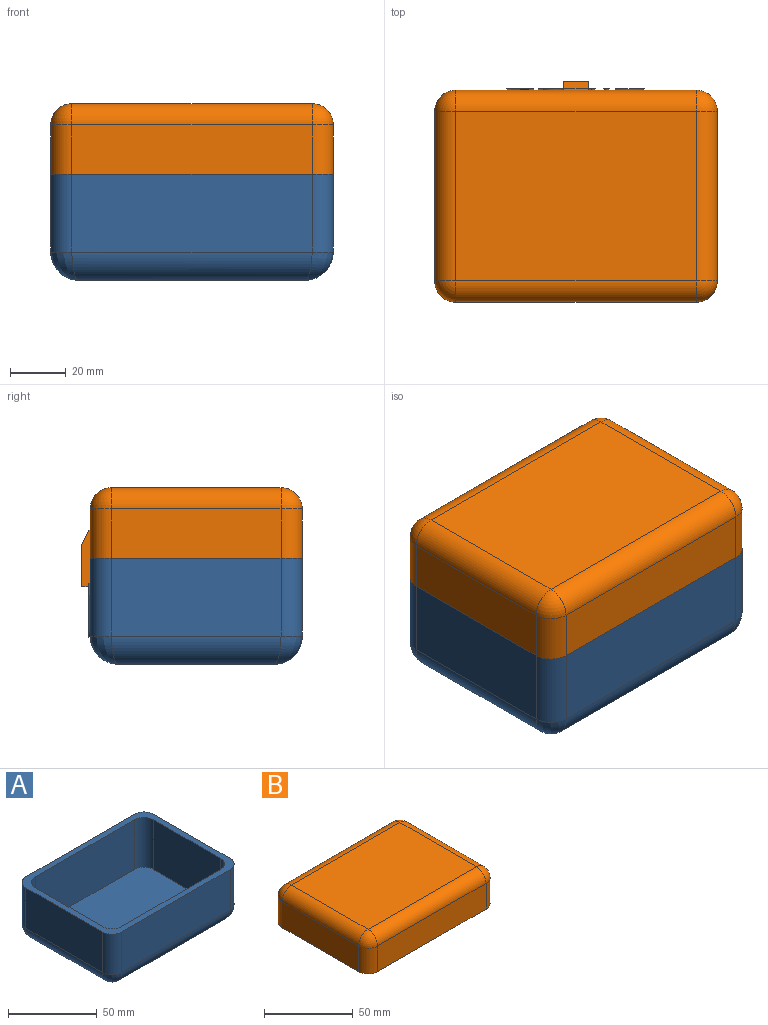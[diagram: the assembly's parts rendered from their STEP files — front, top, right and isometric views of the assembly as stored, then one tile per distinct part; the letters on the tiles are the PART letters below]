
ASSEMBLY  parts=2 mates=1
PART A: 121 faces, bbox 101.6x76.8x38.1 mm
  f0: plane 60.96x27.94mm, normal (1,0,0), area 1703.2mm2, adj f4,f11,f14,f22
  f1: plane 86.36x27.95mm, normal (0,1,0), area 2159.4mm2, adj f4,f11,f12,f19,f27,f29,f30,f31
  f2: plane 60.96x27.94mm, normal (-1,0,0), area 1703.2mm2, adj f4,f12,f13,f23
  f3: plane 86.36x27.94mm, normal (0,-1,0), area 2412.9mm2, adj f4,f13,f14,f26
  f4: plane 101.6x76.2mm, normal (0,0,1), area 1296.8mm2, adj f0,f1,f2,f3,f6,f7,f8,f9
  f5: plane 81.28x55.88mm, normal (0,0,-1), area 4541.9mm2, adj f19,f22,f23,f26
  f6: plane 53.34x34.29mm, normal (-1,0,0), area 1829mm2, adj f4,f10,f16,f18
  f7: plane 78.74x34.29mm, normal (0,-1,0), area 2700mm2, adj f4,f10,f17,f18
  f8: plane 53.34x34.29mm, normal (1,0,0), area 1829mm2, adj f4,f10,f15,f17
  f9: plane 78.74x34.29mm, normal (0,1,0), area 2700mm2, adj f4,f10,f15,f16
  f10: plane 93.98x68.58mm, normal (0,0,1), area 6395.3mm2, adj f6,f7,f8,f9,f15,f16,f17,f18
  f11: cylinder r=7.62mm len=27.94mm, axis (0,0,-1), area 334.4mm2, adj f0,f1,f4,f20
  f12: cylinder r=7.62mm len=27.94mm, axis (0,0,1), area 334.4mm2, adj f1,f2,f4,f21
  f13: cylinder r=7.62mm len=27.94mm, axis (0,0,-1), area 334.4mm2, adj f2,f3,f4,f25
  f14: cylinder r=7.62mm len=27.94mm, axis (0,0,1), area 334.4mm2, adj f0,f3,f4,f24
  f15: cylinder r=7.62mm len=34.29mm, axis (0,0,1), area 410.4mm2, adj f4,f8,f9,f10
  f16: cylinder r=7.62mm len=34.29mm, axis (0,0,-1), area 410.4mm2, adj f4,f6,f9,f10
  f17: cylinder r=7.62mm len=34.29mm, axis (0,0,-1), area 410.4mm2, adj f4,f7,f8,f10
  f18: cylinder r=7.62mm len=34.29mm, axis (0,0,1), area 410.4mm2, adj f4,f6,f7,f10
  f19: cylinder r=10.16mm len=86.36mm, axis (-1,0,0), area 1348.8mm2, adj f1,f5,f20,f21,f103
  f20: bspline ~12.46x10.16mm, area 124.7mm2, adj f11,f19,f22
  f21: bspline ~12.46x10.16mm, area 124.7mm2, adj f12,f19,f23
  f22: cylinder r=10.16mm len=60.96mm, axis (0,1,0), area 943.4mm2, adj f0,f5,f20,f24
  f23: cylinder r=10.16mm len=60.96mm, axis (0,-1,0), area 943.4mm2, adj f2,f5,f21,f25
  f24: bspline ~12.46x10.16mm, area 124.7mm2, adj f14,f22,f26
  f25: bspline ~12.46x10.16mm, area 124.7mm2, adj f13,f23,f26
  f26: cylinder r=10.16mm len=86.36mm, axis (1,0,0), area 1348.8mm2, adj f3,f5,f24,f25
  f27: cone r=2.54mm half-angle=35deg, axis (0,1,0), area 20.4mm2, adj f1,f28
  f28: plane 3.3x3.3mm, normal (0,1,0), area 8.6mm2, adj f27
  f29: extruded ~3.14x0.73mm, area 2.1mm2, adj f1,f30,f43,f44
  f30: plane 1.38x0.68mm, normal (-0.9,0,-0.44), area 1mm2, adj f1,f29,f31,f44
  f31: extruded ~3.8x0.79mm, area 2.5mm2, adj f1,f30,f32,f44
  f32: extruded ~3.55x0.87mm, area 2.3mm2, adj f1,f31,f33,f44
  f33: extruded ~2.47x2.3mm, area 2.2mm2, adj f1,f32,f34,f44
  f34: extruded ~3.74x0.8mm, area 2.4mm2, adj f1,f33,f35,f44
  f35: extruded ~5.26x1.66mm, area 3.6mm2, adj f1,f34,f36,f44
  f36: extruded ~4.71x1.85mm, area 3.3mm2, adj f1,f35,f37,f44
  f37: extruded ~3.54x0.64mm, area 2.3mm2, adj f1,f36,f38,f44
  f38: plane 1.41x0.64mm, normal (-1,0,0), area 0.9mm2, adj f1,f37,f39,f44
  f39: extruded ~3.3x0.64mm, area 2.1mm2, adj f1,f38,f40,f44
  f40: extruded ~3.62x1.48mm, area 2.6mm2, adj f1,f39,f41,f44
  f41: extruded ~4.19x1.27mm, area 2.8mm2, adj f1,f40,f42,f44
  f42: extruded ~4.15x1.32mm, area 2.8mm2, adj f1,f41,f43,f44
  f43: extruded ~3.59x1.52mm, area 2.6mm2, adj f1,f29,f42,f44
  f44: plane 14.2x10.45mm, normal (0,1,0), area 41.7mm2, adj f29,f30,f31,f32,f33,f34,f35,f36
  f45: plane 10.35x0.64mm, normal (-1,0,0), area 6.6mm2, adj f1,f46,f48,f49
  f46: plane 1.57x0.64mm, normal (0,0,1), area 1mm2, adj f1,f45,f47,f49
  f47: plane 10.35x0.64mm, normal (1,0,0), area 6.6mm2, adj f1,f46,f48,f49
  f48: plane 1.57x0.64mm, normal (0,0,-1), area 1mm2, adj f1,f45,f47,f49
  f49: plane 10.35x1.57mm, normal (0,1,0), area 16.2mm2, adj f45,f46,f47,f48
  f50: extruded ~0.79x0.64mm, area 0.5mm2, adj f1,f51,f57,f58
  f51: extruded ~0.66x0.64mm, area 0.5mm2, adj f1,f50,f52,f58
  f52: extruded ~0.65x0.64mm, area 0.5mm2, adj f1,f51,f53,f58
  f53: extruded ~0.79x0.64mm, area 0.5mm2, adj f1,f52,f54,f58
  f54: extruded ~0.78x0.64mm, area 0.5mm2, adj f1,f53,f55,f58
  f55: extruded ~0.65x0.64mm, area 0.5mm2, adj f1,f54,f56,f58
  f56: extruded ~0.66x0.64mm, area 0.5mm2, adj f1,f55,f57,f58
  f57: extruded ~0.79x0.64mm, area 0.5mm2, adj f1,f50,f56,f58
  f58: plane 2.09x1.85mm, normal (0,1,0), area 3.2mm2, adj f50,f51,f52,f53,f54,f55,f56,f57
  f59: plane 1.57x0.64mm, normal (0,0,-1), area 1mm2, adj f1,f60,f75,f76
  f60: plane 6.75x0.64mm, normal (-1,0,0), area 4.3mm2, adj f1,f59,f61,f76
  f61: extruded ~2.89x0.94mm, area 2mm2, adj f1,f60,f62,f76
  f62: extruded ~2.82x0.9mm, area 1.9mm2, adj f1,f61,f63,f76
  f63: extruded ~1.94x0.64mm, area 1.3mm2, adj f1,f62,f64,f76
  f64: extruded ~1.35x1.19mm, area 1.2mm2, adj f1,f63,f65,f76
  f65: plane 0.64x0.08mm, normal (0,0,1), area 0mm2, adj f1,f64,f66,f76
  f66: plane 1.42x0.64mm, normal (-0.98,0,0.18), area 0.9mm2, adj f1,f65,f67,f76
  f67: plane 1.28x0.64mm, normal (0,0,1), area 0.8mm2, adj f1,f66,f68,f76
  f68: plane 10.35x0.64mm, normal (1,0,0), area 6.6mm2, adj f1,f67,f69,f76
  f69: plane 1.57x0.64mm, normal (0,0,-1), area 1mm2, adj f1,f68,f70,f76
  f70: plane 5.43x0.64mm, normal (-1,0,0), area 3.4mm2, adj f1,f69,f71,f76
  f71: extruded ~2.9x0.76mm, area 1.9mm2, adj f1,f70,f72,f76
  f72: extruded ~2.38x0.88mm, area 1.7mm2, adj f1,f71,f73,f76
  f73: extruded ~1.81x0.64mm, area 1.2mm2, adj f1,f72,f74,f76
  f74: extruded ~1.89x0.64mm, area 1.3mm2, adj f1,f73,f75,f76
  f75: plane 6.7x0.64mm, normal (1,0,0), area 4.3mm2, adj f1,f59,f74,f76
  f76: plane 10.54x8.65mm, normal (0,1,0), area 38.8mm2, adj f59,f60,f61,f62,f63,f64,f65,f66
  f77: plane 1.39x0.64mm, normal (0.99,0,-0.15), area 0.9mm2, adj f1,f78,f100,f101
  f78: plane 1.28x0.64mm, normal (0,0,-1), area 0.8mm2, adj f1,f77,f79,f101
  f79: plane 14.7x0.64mm, normal (-1,0,0), area 9.3mm2, adj f1,f78,f80,f101
  f80: plane 1.57x0.64mm, normal (0,0,1), area 1mm2, adj f1,f79,f81,f101
  f81: plane 4.21x0.64mm, normal (1,0,0), area 2.7mm2, adj f1,f80,f82,f101
  f82: plane 0.73x0.64mm, normal (1,0,-0.05), area 0.5mm2, adj f1,f81,f83,f101
  f83: plane 0.75x0.64mm, normal (1,0,-0.09), area 0.5mm2, adj f1,f82,f84,f101
  f84: plane 0.64x0.12mm, normal (0,0,1), area 0.1mm2, adj f1,f83,f85,f101
  f85: extruded ~3.23x1.53mm, area 2.4mm2, adj f1,f84,f86,f101
  f86: extruded ~3.16x1.42mm, area 2.3mm2, adj f1,f85,f87,f101
  f87: extruded ~3.98x1.13mm, area 2.7mm2, adj f1,f86,f88,f101
  f88: extruded ~3.95x1.13mm, area 2.7mm2, adj f1,f87,f89,f101
  f89: extruded ~3.16x1.39mm, area 2.3mm2, adj f1,f88,f90,f101
  f90: extruded ~3.25x1.58mm, area 2.4mm2, adj f1,f89,f100,f101
  f91: extruded ~2.14x1.01mm, area 1.6mm2, adj f92,f99,f101,f102
  f92: extruded ~2.99x0.73mm, area 2mm2, adj f91,f93,f101,f102
  f93: extruded ~3.03x0.73mm, area 2mm2, adj f92,f94,f101,f102
  f94: extruded ~2.11x1.07mm, area 1.6mm2, adj f93,f95,f101,f102
  f95: extruded ~2.34x0.94mm, area 1.7mm2, adj f94,f96,f101,f102
  f96: extruded ~3.14x0.73mm, area 2.1mm2, adj f95,f97,f101,f102
  f97: plane 0.64x0.33mm, normal (1,0,0), area 0.2mm2, adj f96,f98,f101,f102
  f98: extruded ~2.82x0.72mm, area 1.9mm2, adj f97,f99,f101,f102
  f99: extruded ~2.33x0.87mm, area 1.6mm2, adj f91,f98,f101,f102
  f100: plane 0.64x0.08mm, normal (0,0,-1), area 0.1mm2, adj f1,f77,f90,f101
  f101: plane 14.89x9.11mm, normal (0,1,0), area 52.2mm2, adj f77,f78,f79,f80,f81,f82,f83,f84
  f102: plane 8.1x5.91mm, normal (0,1,0), area 40.3mm2, adj f91,f92,f93,f94,f95,f96,f97,f98
  f103: plane 3.03x0.38mm, normal (0,-1,0), area 0.8mm2, adj f19,f104,f105,f106
  f104: plane 1.25x0.64mm, normal (1,0,0), area 0.8mm2, adj f1,f103,f105,f119,f120
  f105: extruded ~1.42x0.64mm, area 0.9mm2, adj f103,f104,f106,f120
  f106: extruded ~2.17x0.73mm, area 1.5mm2, adj f1,f103,f105,f107,f120
  f107: extruded ~2.48x1.54mm, area 1.9mm2, adj f1,f106,f108,f120
  f108: plane 11.79x4.45mm, normal (-0.94,0,-0.35), area 8mm2, adj f1,f107,f109,f120
  f109: plane 1.68x0.64mm, normal (0,0,1), area 1.1mm2, adj f1,f108,f110,f120
  f110: extruded ~7.17x2.57mm, area 4.8mm2, adj f1,f109,f111,f120
  f111: extruded ~1.65x0.64mm, area 1.1mm2, adj f1,f110,f112,f120
  f112: plane 0.64x0.08mm, normal (0,0,1), area 0mm2, adj f1,f111,f113,f120
  f113: extruded ~2.92x0.93mm, area 1.9mm2, adj f1,f112,f114,f120
  f114: plane 5.9x2.27mm, normal (-0.93,0,0.36), area 4mm2, adj f1,f113,f115,f120
  f115: plane 1.68x0.64mm, normal (0,0,1), area 1.1mm2, adj f1,f114,f116,f120
  f116: plane 10.41x4.18mm, normal (0.93,0,-0.37), area 7.1mm2, adj f1,f115,f117,f120
  f117: plane 1.47x0.64mm, normal (0.93,0,0.37), area 1mm2, adj f1,f116,f118,f120
  f118: extruded ~2.31x1.81mm, area 2mm2, adj f1,f117,f119,f120
  f119: extruded ~1.16x0.64mm, area 0.7mm2, adj f1,f104,f118,f120
  f120: plane 15x9.71mm, normal (0,1,0), area 41.6mm2, adj f104,f105,f106,f107,f108,f109,f110,f111
PART B: 36 faces, bbox 101.6x79.2x35.6 mm
  f0: plane 101.6x76.2mm, normal (0,0,-1), area 1296.8mm2, adj f1,f2,f3,f4,f6,f7,f8,f9
  f1: plane 86.36x17.78mm, normal (0,-1,0), area 1535.5mm2, adj f0,f11,f14,f17
  f2: plane 60.96x17.78mm, normal (1,0,0), area 1083.9mm2, adj f0,f11,f12,f16
  f3: plane 86.36x17.78mm, normal (0,1,0), area 1445.2mm2, adj f0,f12,f13,f20,f28,f29,f30
  f4: plane 60.96x17.78mm, normal (-1,0,0), area 1083.9mm2, adj f0,f13,f14,f21
  f5: plane 86.36x60.96mm, normal (0,0,1), area 5264.5mm2, adj f16,f17,f20,f21
  f6: plane 78.74x21.59mm, normal (0,1,0), area 1700mm2, adj f0,f10,f24,f26
  f7: plane 53.34x21.59mm, normal (-1,0,0), area 1151.6mm2, adj f0,f10,f25,f26
  f8: plane 78.74x21.59mm, normal (0,-1,0), area 1700mm2, adj f0,f10,f23,f25
  f9: plane 53.34x21.59mm, normal (1,0,0), area 1151.6mm2, adj f0,f10,f23,f24
  f10: plane 93.98x68.58mm, normal (0,0,-1), area 6395.3mm2, adj f6,f7,f8,f9,f23,f24,f25,f26
  f11: cylinder r=7.62mm len=17.78mm, axis (0,0,-1), area 212.8mm2, adj f0,f1,f2,f15
  f12: cylinder r=7.62mm len=17.78mm, axis (0,0,1), area 212.8mm2, adj f0,f2,f3,f18
  f13: cylinder r=7.62mm len=17.78mm, axis (0,0,-1), area 212.8mm2, adj f0,f3,f4,f22
  f14: cylinder r=7.62mm len=17.78mm, axis (0,0,1), area 212.8mm2, adj f0,f1,f4,f19
  f15: sphere r=7.62mm, area 91.2mm2, adj f11,f16,f17
  f16: cylinder r=7.62mm len=60.96mm, axis (0,-1,0), area 729.7mm2, adj f2,f5,f15,f18
  f17: cylinder r=7.62mm len=86.36mm, axis (-1,0,0), area 1033.7mm2, adj f1,f5,f15,f19
  f18: sphere r=7.62mm, area 91.2mm2, adj f12,f16,f20
  f19: sphere r=7.62mm, area 91.2mm2, adj f14,f17,f21
  f20: cylinder r=7.62mm len=86.36mm, axis (1,0,0), area 1033.7mm2, adj f3,f5,f18,f22
  f21: cylinder r=7.62mm len=60.96mm, axis (0,1,0), area 729.7mm2, adj f4,f5,f19,f22
  f22: sphere r=7.62mm, area 91.2mm2, adj f13,f20,f21
  f23: cylinder r=7.62mm len=21.59mm, axis (0,0,1), area 258.4mm2, adj f0,f8,f9,f10
  f24: cylinder r=7.62mm len=21.59mm, axis (0,0,-1), area 258.4mm2, adj f0,f6,f9,f10
  f25: cylinder r=7.62mm len=21.59mm, axis (0,0,-1), area 258.4mm2, adj f0,f7,f8,f10
  f26: cylinder r=7.62mm len=21.59mm, axis (0,0,1), area 258.4mm2, adj f0,f6,f7,f10
  f27: plane 10.16x8.89mm, normal (0,-1,0), area 70.1mm2, adj f0,f28,f30,f31,f34
  f28: plane 20.32x3.05mm, normal (-1,0,0), area 55.5mm2, adj f3,f27,f29,f31,f32,f33
  f29: plane 8.89x0.51mm, normal (0,0,1), area 4.5mm2, adj f3,f28,f30,f33
  f30: plane 20.32x3.05mm, normal (1,0,0), area 55.5mm2, adj f3,f27,f29,f31,f32,f33
  f31: plane 8.89x3.05mm, normal (0,0,-1), area 27.1mm2, adj f27,f28,f30,f32
  f32: plane 15.24x8.89mm, normal (0,1,0), area 135.5mm2, adj f28,f30,f31,f33
  f33: plane 8.89x5.08mm, normal (0,0.89,0.45), area 50.5mm2, adj f28,f29,f30,f32
  f34: cone r=2.54mm half-angle=35deg, axis (0,1,0), area 20.4mm2, adj f27,f35
  f35: plane 3.3x3.3mm, normal (0,-1,0), area 8.6mm2, adj f34
PLACE A t=(22.92,-3.57,16.68)mm
PLACE B t=(22.92,-3.57,54.78)mm
MATE fastened A.f27 <-> B.f34  axis (0,1,0) through (22.92,33.26,49.7)mm
